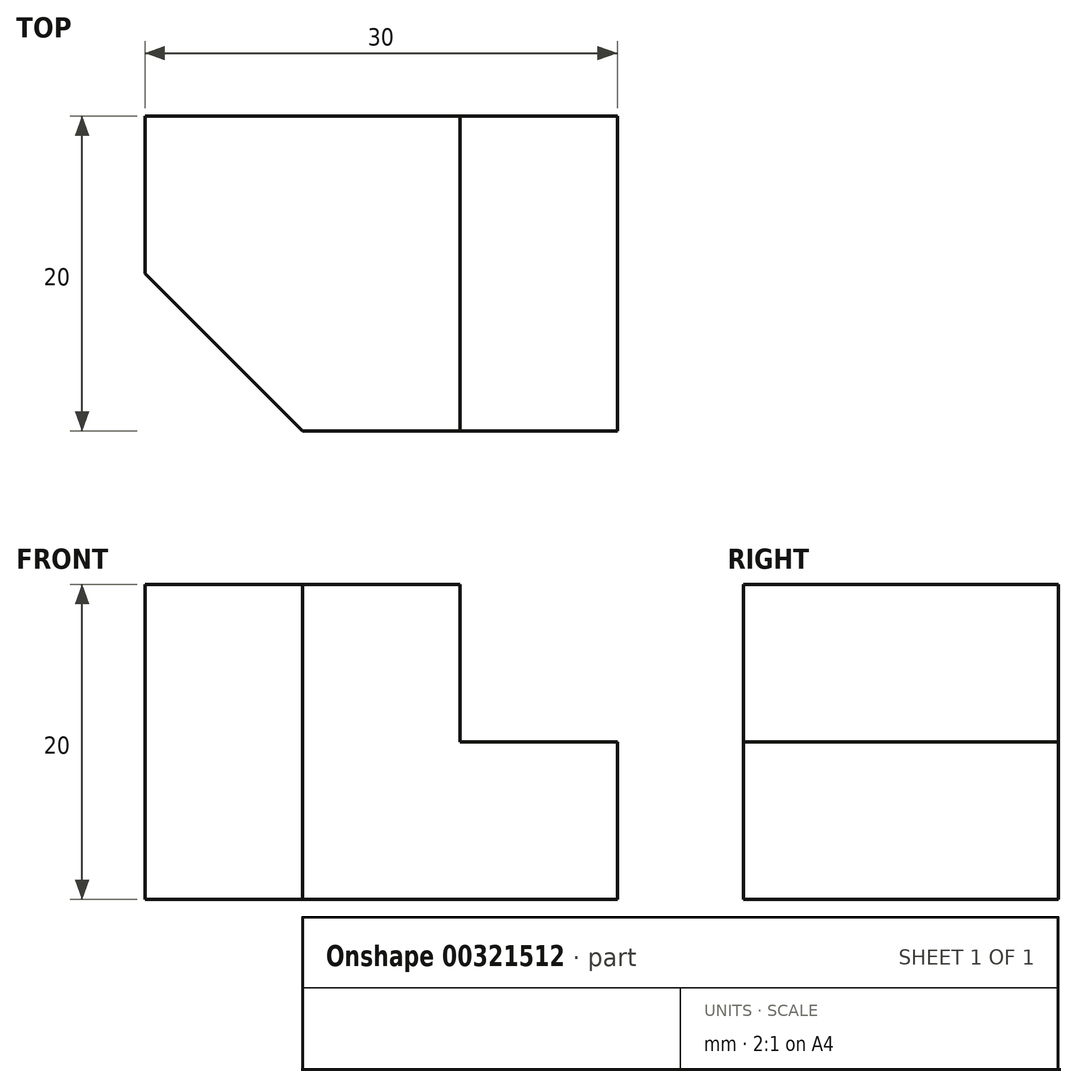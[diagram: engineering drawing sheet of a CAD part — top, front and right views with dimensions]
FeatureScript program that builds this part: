
annotation { "Feature Type Name" : "Feature", "Feature Type Description" : "" }
export const myFeature = defineFeature(function(context is Context, id is Id, definition is map)
    precondition{}
    {
        {
            var Q0;
            Q0=qCreatedBy(makeId("Front.planeOp"),FACE);
            var sketch = newSketch(context, id + "F0", { "sketchPlane" : qUnion([Q0])});
            skLineSegment(sketch, "E0", {"start": v(0, 0) * mm, "end": v(0, 20) * mm});
            skLineSegment(sketch, "E1", {"start": v(0, 20) * mm, "end": v(10, 20) * mm});
            skLineSegment(sketch, "E2", {"start": v(10, 20) * mm, "end": v(10, 0) * mm});
            skLineSegment(sketch, "E3", {"start": v(10, 0) * mm, "end": v(0, 0) * mm});
            skLineSegment(sketch, "E4", {"start": v(10, 20) * mm, "end": v(20, 20) * mm});
            skLineSegment(sketch, "E5", {"start": v(20, 20) * mm, "end": v(20, 10) * mm});
            skLineSegment(sketch, "E6", {"start": v(20, 10) * mm, "end": v(30, 10) * mm});
            skLineSegment(sketch, "E7", {"start": v(30, 10) * mm, "end": v(30, 0) * mm});
            skLineSegment(sketch, "E8", {"start": v(30, 0) * mm, "end": v(10, 0) * mm});
            skSolve(sketch);
        }
        {
            var Q0;
            Q0=makeQuery(id+"F0.imprint","IMPRINT",FACE,{"disambiguationData":[TD([[makeQuery(id+"F0.imprint","IMPRINT",EDGE,{"derivedFrom":sQuery(id+"F0.wireOp",EDGE,"E0")}),-1.0]])]});
            var Q1;
            Q1=makeQuery(id+"F0.imprint","IMPRINT",FACE,{"disambiguationData":[TD([[makeQuery(id+"F0.imprint","IMPRINT",EDGE,{"derivedFrom":sQuery(id+"F0.wireOp",EDGE,"E2")}),1.0]])]});
            extrude(context, id + "F1", {"entities" : qUnion([Q0, Q1]), "depth" : 20 * mm});
        }
        {
            var Q0;
            Q0=makeQuery(id+"F1.opExtrude","SWEPT_FACE",FACE,{"disambiguationData":[OSD([sQuery(id+"F0.wireOp",EDGE,"E1"),sQuery(id+"F0.wireOp",EDGE,"E4")])]});
            var sketch = newSketch(context, id + "F2", { "sketchPlane" : qUnion([Q0])});
            skLineSegment(sketch, "E9", {"start": v(0, -10) * mm, "end": v(10, -20) * mm});
            skLineSegment(sketch, "E10", {"start": v(10, -20) * mm, "end": v(0, -20) * mm});
            skLineSegment(sketch, "E11", {"start": v(0, -20) * mm, "end": v(0, -10) * mm});
            skSolve(sketch);
        }
        {
            var Q0;
            Q0=makeQuery(id+"F2.imprint","IMPRINT",FACE,{"disambiguationData":[TD([[makeQuery(id+"F2.imprint","IMPRINT",EDGE,{"derivedFrom":sQuery(id+"F2.wireOp",EDGE,"E9")}),-1.0]])]});
            extrude(context, id + "F3", {"entities" : qUnion([Q0]), "operationType" : NewBodyOperationType.REMOVE, "endBound" : BoundingType.THROUGH_ALL, "oppositeDirection" : true, "depth" : 25 * mm});
        }
    });
